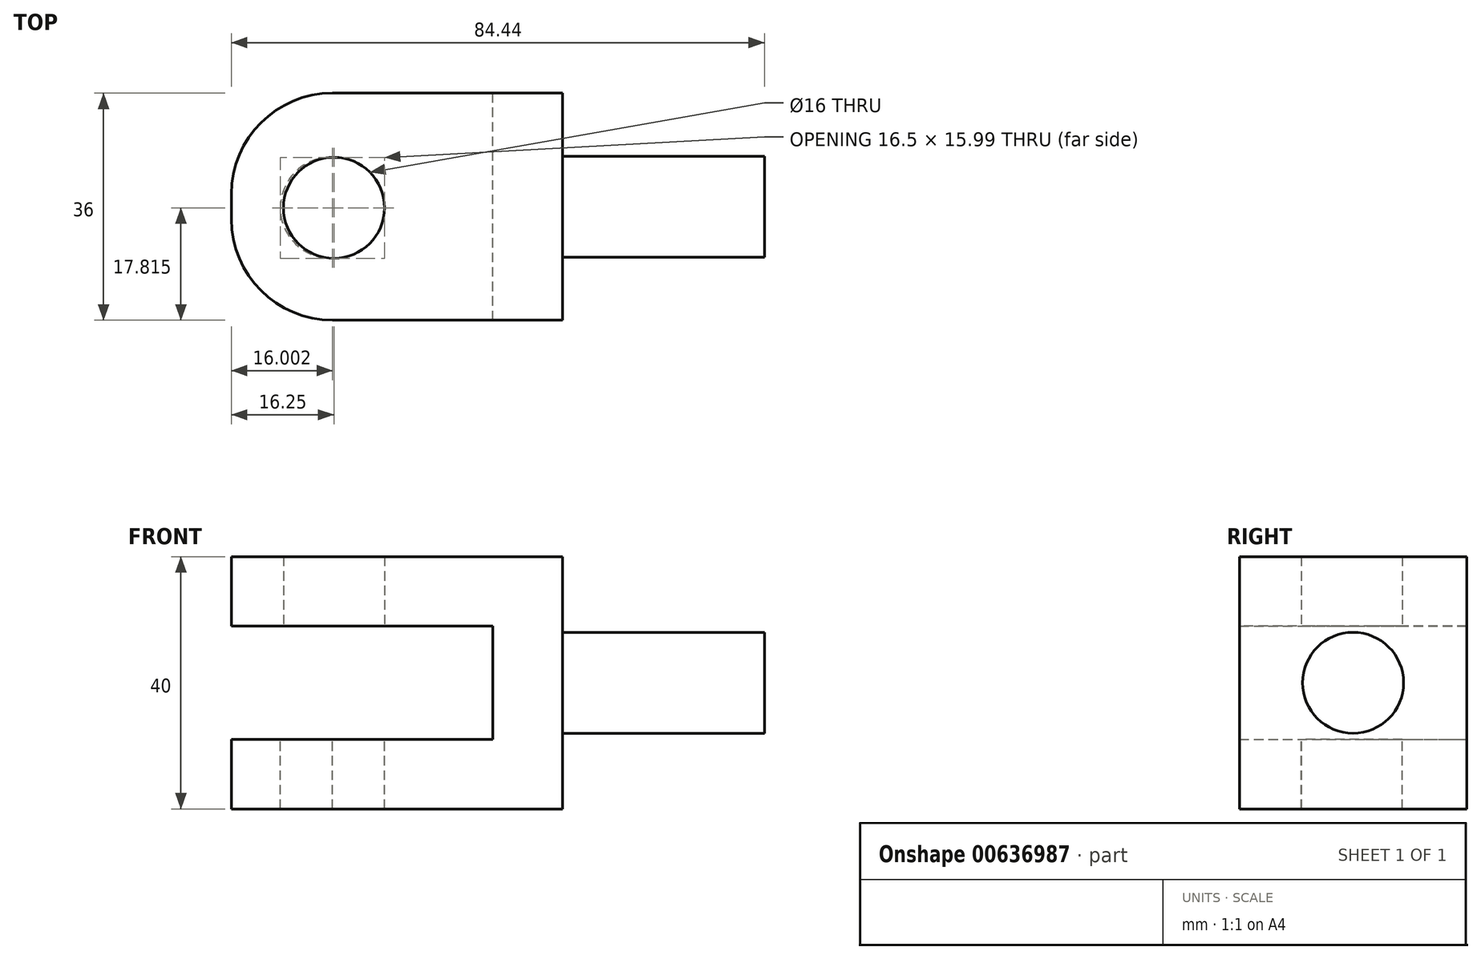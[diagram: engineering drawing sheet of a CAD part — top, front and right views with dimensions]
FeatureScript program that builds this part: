
annotation { "Feature Type Name" : "Feature", "Feature Type Description" : "" }
export const myFeature = defineFeature(function(context is Context, id is Id, definition is map)
    precondition{}
    {
        {
            var Q0;
            Q0=qCreatedBy(makeId("Front.planeOp"),FACE);
            var sketch = newSketch(context, id + "F0", { "sketchPlane" : qUnion([Q0])});
            skLineSegment(sketch, "E0", {"start": v(-33.23, 11) * mm, "end": v(-33.23, 0) * mm});
            skLineSegment(sketch, "E1", {"start": v(-33.23, 0) * mm, "end": v(8.21, 0) * mm});
            skLineSegment(sketch, "E2", {"start": v(8.21, 0) * mm, "end": v(8.21, -18) * mm});
            skLineSegment(sketch, "E3", {"start": v(8.21, -18) * mm, "end": v(-33.23, -18) * mm});
            skLineSegment(sketch, "E4", {"start": v(-33.23, -18) * mm, "end": v(-33.23, -29) * mm});
            skLineSegment(sketch, "E5", {"start": v(-33.23, -29) * mm, "end": v(19.21, -29) * mm});
            skLineSegment(sketch, "E6", {"start": v(-33.23, 11) * mm, "end": v(19.21, 11) * mm});
            skLineSegment(sketch, "E7", {"start": v(19.21, 11) * mm, "end": v(19.21, 0) * mm});
            skLineSegment(sketch, "E8", {"start": v(19.21, 0) * mm, "end": v(19.21, -18) * mm});
            skLineSegment(sketch, "E9", {"start": v(19.21, -18) * mm, "end": v(19.21, -29) * mm});
            skSolve(sketch);
        }
        {
            var Q0;
            Q0=makeQuery(id+"F0.imprint","IMPRINT",FACE,{"disambiguationData":[TD([[makeQuery(id+"F0.imprint","IMPRINT",EDGE,{"derivedFrom":sQuery(id+"F0.wireOp",EDGE,"E0")}),1.0]])]});
            extrude(context, id + "F1", {"entities" : qUnion([Q0]), "depth" : 36 * mm, "offsetDistance" : 25 * mm});
        }
        {
            var Q0;
            Q0=makeQuery(id+"F1.opExtrude","SWEPT_FACE",FACE,{"disambiguationData":[OSD([sQuery(id+"F0.wireOp",EDGE,"E7"),sQuery(id+"F0.wireOp",EDGE,"E8"),sQuery(id+"F0.wireOp",EDGE,"E9")])]});
            var sketch = newSketch(context, id + "F2", { "sketchPlane" : qUnion([Q0])});
            skPoint(sketch, "E10", {"position": v(-18, -9) * mm});
            skPoint(sketch, "E10.positionSnap0", {"position": v(-18, 11) * mm});
            skPoint(sketch, "E10.positionSnap1", {"position": v(0, -9) * mm});
            skCircle(sketch, "E11", {"center": v(-18, -9) * mm, "radius": 8 * mm});
            skSolve(sketch);
        }
        {
            var Q0;
            Q0 = qSketchRegion(id + "F2", true);
            extrude(context, id + "F3", {"entities" : qUnion([Q0]), "operationType" : NewBodyOperationType.ADD, "depth" : 32 * mm, "offsetDistance" : 25 * mm});
        }
        {
            var Q0;
            Q0=qCreatedBy(makeId("Top.planeOp"),FACE);
            var sketch = newSketch(context, id + "F4", { "sketchPlane" : qUnion([Q0])});
            skPoint(sketch, "E12", {"position": v(-16.98, -18.18) * mm});
            skCircle(sketch, "E13", {"center": v(-16.98, -18.18) * mm, "radius": 8 * mm});
            skSolve(sketch);
        }
        {
            var Q0;
            Q0 = qSketchRegion(id + "F4", true);
            extrude(context, id + "F5", {"entities" : qUnion([Q0]), "operationType" : NewBodyOperationType.REMOVE, "endBound" : BoundingType.THROUGH_ALL, "oppositeDirection" : true, "depth" : 11 * mm, "offsetDistance" : 25 * mm});
        }
        {
            var Q0;
            Q0=qCreatedBy(makeId("Top.planeOp"),FACE);
            var sketch = newSketch(context, id + "F6", { "sketchPlane" : qUnion([Q0])});
            skPoint(sketch, "E14", {"position": v(-17.48, -18.18) * mm});
            skCircle(sketch, "E15", {"center": v(-17.48, -18.18) * mm, "radius": 8 * mm});
            skSolve(sketch);
        }
        {
            var Q0;
            Q0 = qSketchRegion(id + "F6", true);
            extrude(context, id + "F7", {"entities" : qUnion([Q0]), "operationType" : NewBodyOperationType.REMOVE, "endBound" : BoundingType.THROUGH_ALL, "oppositeDirection" : true, "depth" : 11 * mm, "offsetDistance" : 25 * mm});
        }
        {
            var Q0;
            Q0=sQuery(id+"F4.wireOp",VERTEX,"E12");
            var Q1;
            Q1=makeQuery(id+"F1.opExtrude","SWEPT_BODY",BODY,{"disambiguationData":[OSD([sQuery(id+"F0.wireOp",EDGE,"E0"),sQuery(id+"F0.wireOp",EDGE,"E1"),sQuery(id+"F0.wireOp",EDGE,"E2"),sQuery(id+"F0.wireOp",EDGE,"E3"),sQuery(id+"F0.wireOp",EDGE,"E4"),sQuery(id+"F0.wireOp",EDGE,"E5"),sQuery(id+"F0.wireOp",EDGE,"E6"),sQuery(id+"F0.wireOp",EDGE,"E7"),sQuery(id+"F0.wireOp",EDGE,"E8"),sQuery(id+"F0.wireOp",EDGE,"E9")])]});
            hole(context, id + "F8", {"style" : HoleStyle.SIMPLE, "endStyle" : HoleEndStyle.THROUGH, "oppositeDirection" : true, "holeDiameter" : 16 * mm, "majorDiameter" : 5 * mm, "isTappedThrough" : true, "tappedDepth" : 12 * mm, "tapClearance" : 3, "locations" : qUnion([Q0]), "scope" : qUnion([Q1])});
        }
        {
            var Q0;
            Q0=makeQuery(id+"F1.opExtrude","CAP_EDGE",EDGE,{"disambiguationData":[OSD([sQuery(id+"F0.wireOp",EDGE,"E4")])],"isStart":true});
            var Q1;
            Q1=makeQuery(id+"F1.opExtrude","CAP_EDGE",EDGE,{"disambiguationData":[OSD([sQuery(id+"F0.wireOp",EDGE,"E0")])],"isStart":true});
            var Q2;
            Q2=makeQuery(id+"F1.opExtrude","CAP_EDGE",EDGE,{"disambiguationData":[OSD([sQuery(id+"F0.wireOp",EDGE,"E0")])],"isStart":false});
            var Q3;
            Q3=makeQuery(id+"F1.opExtrude","CAP_EDGE",EDGE,{"disambiguationData":[OSD([sQuery(id+"F0.wireOp",EDGE,"E4")])],"isStart":false});
            fillet(context, id + "F9", {"entities" : qUnion([Q0, Q1, Q2, Q3]), "radius" : 16 * mm, "tangentPropagation" : true, "allowEdgeOverflow" : false});
        }
    });
